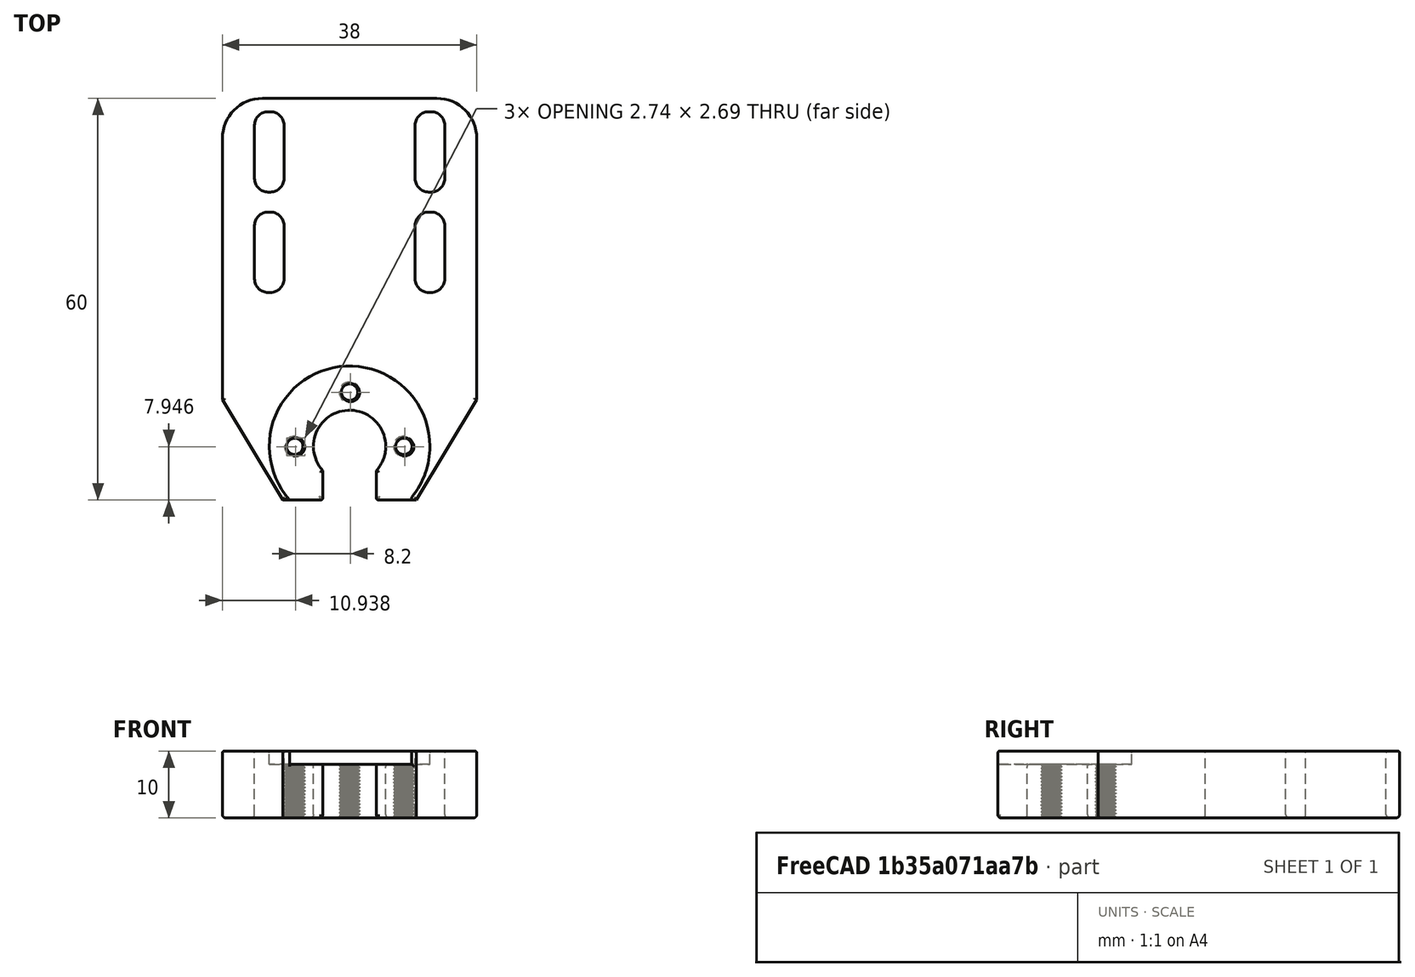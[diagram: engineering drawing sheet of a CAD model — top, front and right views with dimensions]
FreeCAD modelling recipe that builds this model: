
FCSTD DOCUMENT  (FreeCAD 0.18R16131 (Git))
Label: YDriveLagerAntrieb_Ver2
License: All rights reserved
LicenseURL: http://en.wikipedia.org/wiki/All_rights_reserved
objects: Part::Cut×10, Part::Fillet×7, Part::Box×6, Part::Feature×3, Part::Cylinder×2, Part::Chamfer×1
note: 29 computed .brp shape members not serialized (recipe doc carries the construction recipe); baked Part::Feature solids carry a one-line shape summary decoded from their .brp

FEATURE [Part::Box] Box  label="Würfel"
  AttacherType = Attacher::AttachEngine3D
  Height = 10
  Length = 38
  Placement = pos=(-19,-6,0) rot=(0,0,1;0rad)
  Width = 60
FEATURE [Part::Cylinder] Cylinder  label="Zylinder"
  Angle = 360
  AttacherType = Attacher::AttachEngine3D
  Height = 20
  Placement = pos=(0,2,8) rot=(0,0,1;0rad)
  Radius = 12
FEATURE [Part::Box] Box003  label="Würfel003"
  AttacherType = Attacher::AttachEngine3D
  Height = 20
  Length = 4.4
  Placement = pos=(9.8,25,0) rot=(0,0,1;0rad)
  Width = 12
FEATURE [Part::Box] Box004  label="Würfel004"
  AttacherType = Attacher::AttachEngine3D
  Height = 20
  Length = 4.4
  Placement = pos=(-14.2,25,0) rot=(0,0,1;0rad)
  Width = 12
FEATURE [Part::Box] Box005  label="Würfel005"
  AttacherType = Attacher::AttachEngine3D
  Height = 20
  Length = 4.4
  Placement = pos=(9.8,40,0) rot=(0,0,1;0rad)
  Width = 12
FEATURE [Part::Box] Box006  label="Würfel006"
  AttacherType = Attacher::AttachEngine3D
  Height = 20
  Length = 4.4
  Placement = pos=(-14.2,40,0) rot=(0,0,1;0rad)
  Width = 12
FEATURE [Part::Fillet] Fillet
  Base = -> Box006
  Edges = 4 edges r=2: [Edge1,Edge3,Edge5,Edge7]
FEATURE [Part::Fillet] Fillet001
  Base = -> Box005
  Edges = 4 edges r=2: [Edge1,Edge3,Edge5,Edge7]
FEATURE [Part::Fillet] Fillet002
  Base = -> Box003
  Edges = 4 edges r=2: [Edge1,Edge3,Edge5,Edge7]
FEATURE [Part::Fillet] Fillet003
  Base = -> Box004
  Edges = 4 edges r=2: [Edge1,Edge3,Edge5,Edge7]
FEATURE [Part::Feature] Part__Feature001  label="ScrewTap-M3x30_001"
  Placement = pos=(-8.2,2,21.5) rot=(0,0,1;0rad)
  shape: bbox 4.303 x 4.617 x 31.5 mm, 250 faces (baked)
FEATURE [Part::Feature] Part__Feature002  label="ScrewTap-M3x30_002"
  Placement = pos=(0,10.1,21.5) rot=(0,0,1;0rad)
  shape: bbox 4.303 x 4.617 x 31.5 mm, 250 faces (baked)
FEATURE [Part::Feature] Part__Feature003  label="ScrewTap-M3x30_003"
  Placement = pos=(8.1,2,21.5) rot=(0,0,1;0rad)
  shape: bbox 4.303 x 4.617 x 31.5 mm, 250 faces (baked)
FEATURE [Part::Cylinder] Cylinder001  label="Zylinder001"
  Angle = 360
  AttacherType = Attacher::AttachEngine3D
  Height = 20
  Placement = pos=(0,2,0) rot=(0,0,1;0rad)
  Radius = 5.4
FEATURE [Part::Box] Box008  label="Würfel008"
  AttacherType = Attacher::AttachEngine3D
  Height = 10
  Length = 8
  Placement = pos=(-4,-9,0) rot=(0,0,1;0rad)
  Width = 8
FEATURE [Part::Chamfer] Chamfer
  Base = -> Box
  Edges = 2 edges: [Edge1 r1=15 r2=9,Edge5 r1=15 r2=9]
FEATURE [Part::Fillet] Fillet004
  Base = -> Chamfer
  Edges = 2 edges r=6: [Edge3,Edge13]
FEATURE [Part::Cut] Cut
  Base = -> Fillet004
  Tool = -> Fillet
FEATURE [Part::Cut] Cut001
  Base = -> Cut
  Tool = -> Fillet001
FEATURE [Part::Cut] Cut002
  Base = -> Cut001
  Tool = -> Fillet002
FEATURE [Part::Cut] Cut003
  Base = -> Cut002
  Tool = -> Fillet003
FEATURE [Part::Cut] Cut004
  Base = -> Cut003
  Tool = -> Cylinder
FEATURE [Part::Cut] Cut005
  Base = -> Cut004
  Tool = -> Cylinder001
FEATURE [Part::Cut] Cut006
  Base = -> Cut005
  Tool = -> Box008
FEATURE [Part::Cut] Cut007
  Base = -> Cut006
  Tool = -> Part__Feature003
FEATURE [Part::Cut] Cut008
  Base = -> Cut007
  Tool = -> Part__Feature002
FEATURE [Part::Cut] Cut009
  Base = -> Cut008
  Tool = -> Part__Feature001
FEATURE [Part::Fillet] Fillet005
  Base = -> Cut009
  Edges = 45 edges r=0.5: [Edge4,Edge47,Edge49,Edge51,Edge52,Edge53,Edge54,Edge55,Edge56,Edge57,Edge58,Edge59,Edge60,Edge61,Edge62,Edge63,Edge64,Edge65,Edge66,Edge67,Edge68,Edge69,Edge70,Edge71,Edge72,Edge73,Edge74,Edge75,Edge76,Edge77,Edge78,Edge79,Edge80,Edge81,Edge82,Edge83,Edge84,Edge85,Edge86,Edge87,Edge88,Edge89,Edge90,+2 more]
FEATURE [Part::Fillet] Fillet006
  Base = -> Fillet005
  Edges = 51 edges r=0.3: [Edge3,Edge6,Edge11,Edge12,Edge13,Edge14,Edge15,Edge16,Edge17,Edge18,Edge19,Edge20,Edge21,Edge22,Edge23,Edge24,Edge25,Edge26,Edge27,Edge28,Edge29,Edge30,Edge31,Edge32,Edge33,Edge34,Edge35,Edge36,Edge37,Edge38,Edge39,Edge40,Edge41,Edge42,Edge43,Edge44,Edge45,Edge46,Edge47,Edge48,Edge49,Edge50,Edge51,+8 more]
